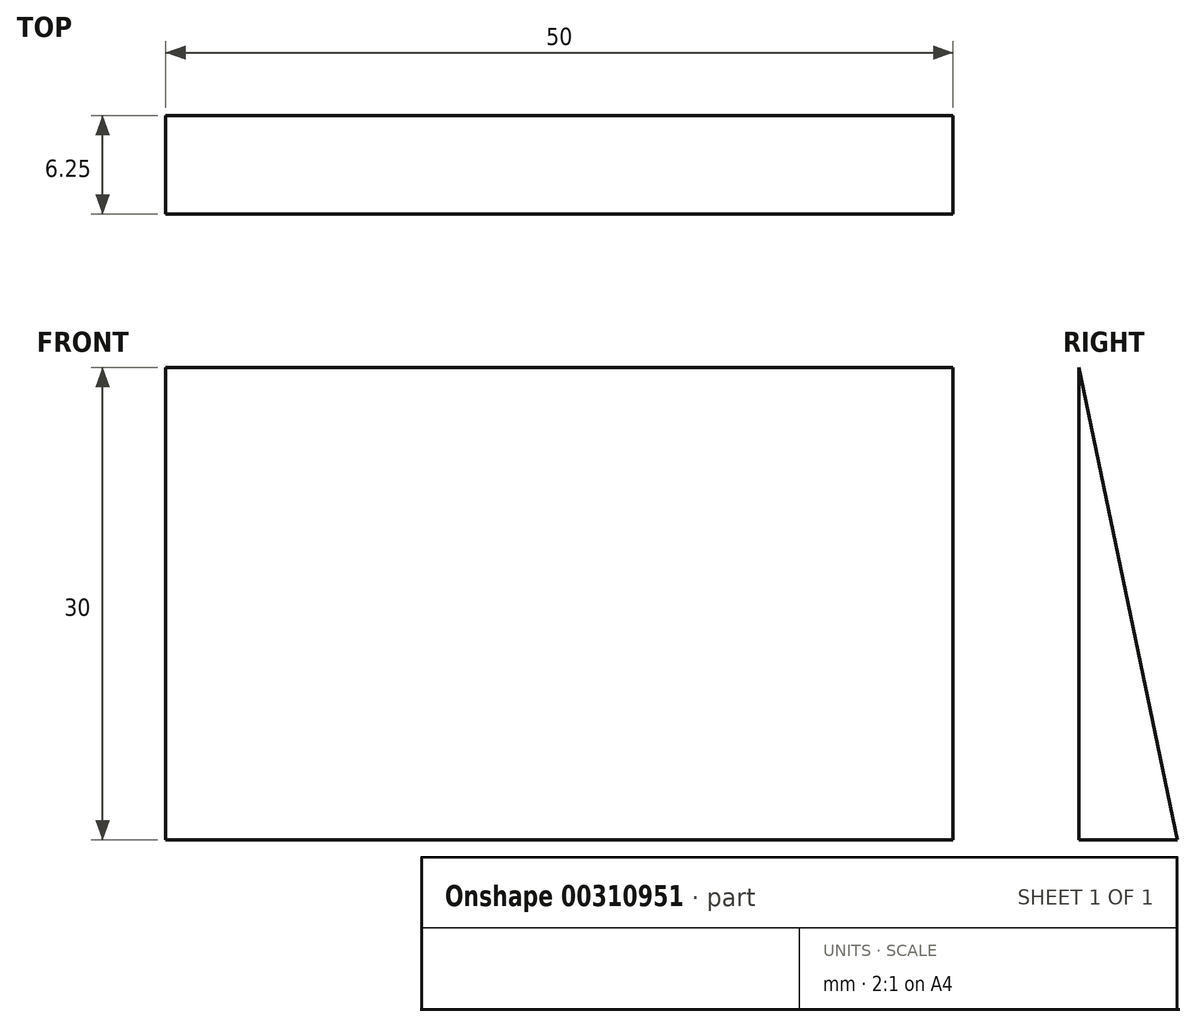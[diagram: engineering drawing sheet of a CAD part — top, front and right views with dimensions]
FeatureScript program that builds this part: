
annotation { "Feature Type Name" : "Feature", "Feature Type Description" : "" }
export const myFeature = defineFeature(function(context is Context, id is Id, definition is map)
    precondition{}
    {
        {
            var Q0;
            Q0=qCreatedBy(makeId("Right.planeOp"),FACE);
            var sketch = newSketch(context, id + "F0", { "sketchPlane" : qUnion([Q0])});
            skLineSegment(sketch, "E0", {"start": v(0, 0) * mm, "end": v(0, 30) * mm});
            skLineSegment(sketch, "E1", {"start": v(0, 30) * mm, "end": v(6.25, 0) * mm});
            skLineSegment(sketch, "E2", {"start": v(6.25, 0) * mm, "end": v(0, 0) * mm});
            skSolve(sketch);
        }
        {
            var Q0;
            Q0 = qSketchRegion(id + "F0", true);
            extrude(context, id + "F1", {"entities" : qUnion([Q0]), "depth" : 50 * mm});
        }
    });
